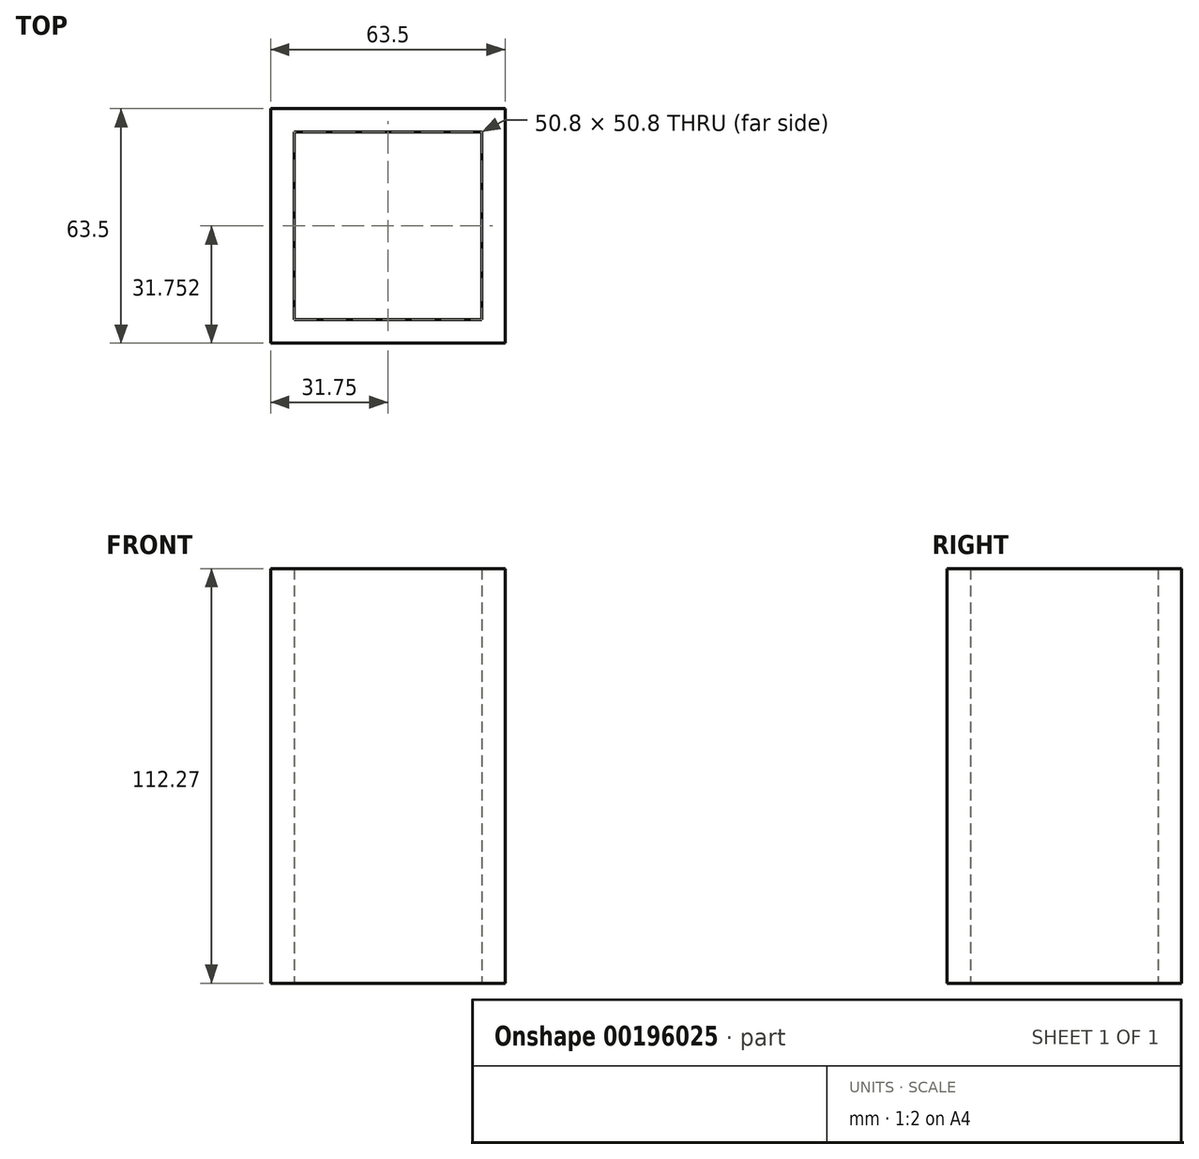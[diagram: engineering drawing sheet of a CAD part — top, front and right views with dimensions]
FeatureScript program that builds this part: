
annotation { "Feature Type Name" : "Feature", "Feature Type Description" : "" }
export const myFeature = defineFeature(function(context is Context, id is Id, definition is map)
    precondition{}
    {
        {
            var Q0;
            Q0=qCreatedBy(makeId("Top.planeOp"),FACE);
            var sketch = newSketch(context, id + "F0", { "sketchPlane" : qUnion([Q0])});
            skLineSegment(sketch, "E0.bottom", {"start": v(-37.6, 12.35) * mm, "end": v(25.9, 12.35) * mm});
            skLineSegment(sketch, "E0.top", {"start": v(-37.6, -51.15) * mm, "end": v(25.9, -51.15) * mm});
            skLineSegment(sketch, "E0.left", {"start": v(-37.6, 12.35) * mm, "end": v(-37.6, -51.15) * mm});
            skLineSegment(sketch, "E0.right", {"start": v(25.9, 12.35) * mm, "end": v(25.9, -51.15) * mm});
            skLineSegment(sketch, "E1.0", {"start": v(-31.24, -44.8) * mm, "end": v(19.56, -44.8) * mm});
            skLineSegment(sketch, "E1.1", {"start": v(-31.24, 6) * mm, "end": v(-31.24, -44.8) * mm});
            skLineSegment(sketch, "E1.2", {"start": v(-31.24, 6) * mm, "end": v(19.56, 6) * mm});
            skLineSegment(sketch, "E1.3", {"start": v(19.56, 6) * mm, "end": v(19.56, -44.8) * mm});
            skSolve(sketch);
        }
        {
            var Q0;
            Q0 = qSketchRegion(id + "F0", true);
            extrude(context, id + "F1", {"entities" : qUnion([Q0]), "depth" : 112.27 * mm});
        }
    });
